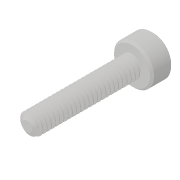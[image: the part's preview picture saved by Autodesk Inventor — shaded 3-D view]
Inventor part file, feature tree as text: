
AUTODESK INVENTOR PART (.ipt)
format: ipt  version: 2018 (Build 220112000, 112)  size: 892,928 bytes
history: native  units: in
note: dims shown in document units (in); Inventor stores cm internally (conversion verified against a paired STEP export)
features: chamfer x1
ambient origin geometry x8: Origin, YZ Plane, XZ Plane, XY Plane, X Axis, Y Axis, Z Axis, Center Point
bodies: Solid1 (feature_tree)
feature tree (1):
  chamfer  "Chamfer1"  [1 undecoded]
note: 1 required parameter value undecoded (feature->parameter linkage not recoverable at this tier; creation-order binding heuristic only, values carry confidence <= 0.55)
